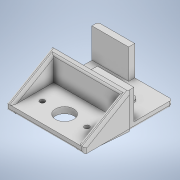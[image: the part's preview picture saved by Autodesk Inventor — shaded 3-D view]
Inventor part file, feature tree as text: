
AUTODESK INVENTOR PART (.ipt)
format: ipt  version: 2022 (Build 260153000, 153)  size: 306,688 bytes
history: native  units: in
note: dims shown in document units (in); Inventor stores cm internally (conversion verified against a paired STEP export)
features: extrude x11, sketch x11, chamfer x3, fillet x1
ambient origin geometry x8: Origin, YZ Plane, XZ Plane, XY Plane, X Axis, Y Axis, Z Axis, Center Point
bodies: Solid1 (feature_tree)
feature tree (26):
  extrude  "Extrusion1"  Depth=1.4331in
  extrude  "Extrusion2"  Depth=1.1811in
  extrude  "Extrusion3"  Depth=1.1811in
  extrude  "Extrusion4"  Depth=0.9606in TaperAngle=0.0deg
  extrude  "Extrusion5"  Depth=0.1181in
  chamfer  "Chamfer1"  Distance=0.1181in
  extrude  "Extrusion12"  Depth=0.1575in
  extrude  "Extrusion13"  Depth=0.2362in
  extrude  "Extrusion14"  Depth=0.1181in TaperAngle=0.0deg
  extrude  "Extrusion15"  Depth=2.5197in
  extrude  "Extrusion16"  Depth=0.1969in
  extrude  "Extrusion17"  Depth=0.1969in
  chamfer  "Chamfer4"  Distance=0.1181in
  chamfer  "Chamfer5"  Distance=0.1969in
  fillet  "Fillet3"  Radius=0.1969in
  sketch  "Sketch1"  dims[d0=2.3937in d1=1.4331in]
  sketch  "Sketch2"  dims[d2=0.1969in d3=0.0in d4=1.1811in]
  sketch  "Sketch3"  dims[d5=0.1969in d6=1.1811in]
  sketch  "Sketch4"  dims[d7=0.1969in d8=0.9606in d9=0.0in]
  sketch  "Sketch5"  dims[d10=0.3406in d11=0.3406in d12=0.1181in d13=0.0in]
  sketch  "Sketch12"  dims[d14=0.1575in d15=0.1575in]
  sketch  "Sketch13"  dims[d16=0.5906in d17=0.0in d18=0.2362in]
  sketch  "Sketch14"  dims[d19=0.2362in d20=0.1181in d21=0.0in]
  sketch  "Sketch15"  dims[d22=0.0591in d23=0.0787in d24=45.0deg d60=2.5197in]
  sketch  "Sketch16"  dims[d61=0.1969in d62=0.1969in]
  sketch  "Sketch17"  dims[d63=0.1181in d64=0.1969in d65=0.1181in d66=0.1969in d67=0.1969in d68=1.4508in d69=0.0in d70=0.5906in d71=0.1575in d72=0.1575in d73=1.4508in d74=0.0in d75=0.1181in d76=0.8425in d77=0.0in d78=3.5433in d79=0.0in d80=0.0787in d81=0.0in d82=0.0787in d83=1.9685in d84=0.0in d85=0.0472in d86=0.0787in d87=45.0deg d88=0.0472in d89=0.0787in d90=45.0deg d91=0.0787in]
